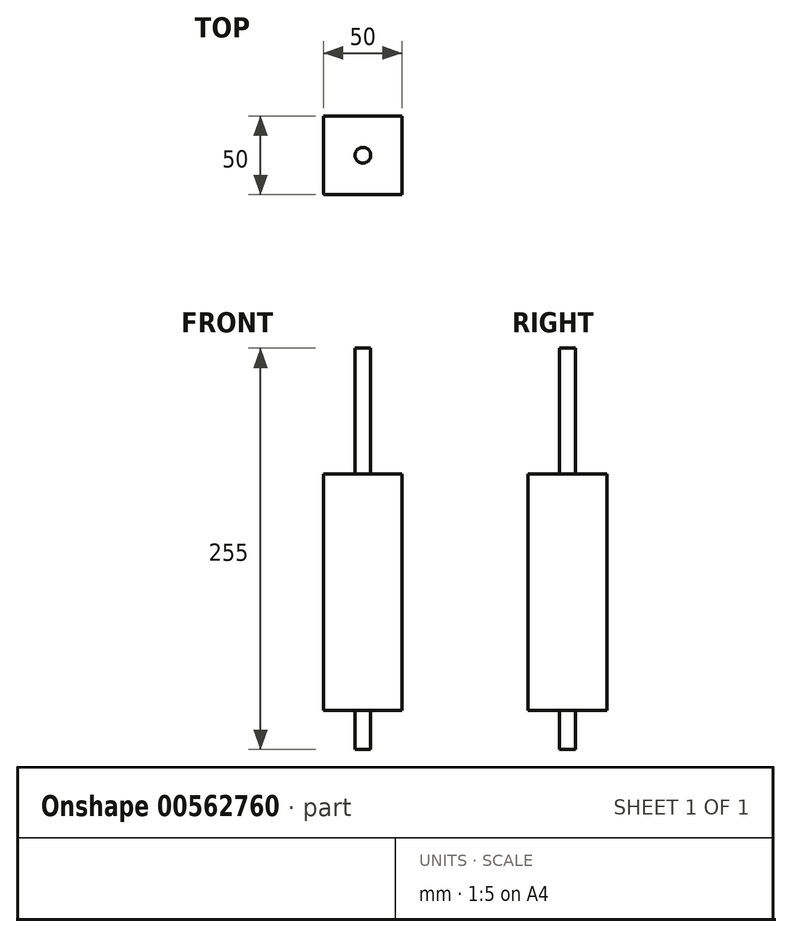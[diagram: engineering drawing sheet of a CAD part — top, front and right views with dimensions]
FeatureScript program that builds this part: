
annotation { "Feature Type Name" : "Feature", "Feature Type Description" : "" }
export const myFeature = defineFeature(function(context is Context, id is Id, definition is map)
    precondition{}
    {
        {
            var Q0;
            Q0=qCreatedBy(makeId("Top.planeOp"),FACE);
            var sketch = newSketch(context, id + "F0", { "sketchPlane" : qUnion([Q0])});
            skLineSegment(sketch, "E0.bottom", {"start": v(25, 25) * mm, "end": v(-25, 25) * mm});
            skLineSegment(sketch, "E0.top", {"start": v(25, -25) * mm, "end": v(-25, -25) * mm});
            skLineSegment(sketch, "E0.left", {"start": v(25, 25) * mm, "end": v(25, -25) * mm});
            skLineSegment(sketch, "E0.right", {"start": v(-25, 25) * mm, "end": v(-25, -25) * mm});
            skPoint(sketch, "E0.middle", {"position": v(0, 0) * mm});
            skSolve(sketch);
        }
        {
            var Q0;
            Q0=makeQuery(id+"F0.imprint","IMPRINT",FACE,{"disambiguationData":[TD([[makeQuery(id+"F0.imprint","IMPRINT",EDGE,{"derivedFrom":sQuery(id+"F0.wireOp",EDGE,"E0.bottom")}),1.0]])]});
            extrude(context, id + "F1", {"entities" : qUnion([Q0]), "endBound" : BoundingType.SYMMETRIC, "depth" : 150 * mm, "offsetDistance" : 25 * mm});
        }
        {
            var Q0;
            Q0=makeQuery(id+"F1.opExtrude","CAP_FACE",FACE,{"disambiguationData":[OSD([sQuery(id+"F0.wireOp",EDGE,"E0.bottom"),sQuery(id+"F0.wireOp",EDGE,"E0.top"),sQuery(id+"F0.wireOp",EDGE,"E0.left"),sQuery(id+"F0.wireOp",EDGE,"E0.right")])],"isStart":false});
            var sketch = newSketch(context, id + "F2", { "sketchPlane" : qUnion([Q0])});
            skCircle(sketch, "E1", {"center": v(0, 0) * mm, "radius": 5 * mm});
            skSolve(sketch);
        }
        {
            var Q0;
            Q0 = qSketchRegion(id + "F2", true);
            extrude(context, id + "F3", {"entities" : qUnion([Q0]), "operationType" : NewBodyOperationType.ADD, "depth" : 80 * mm, "offsetDistance" : 25 * mm});
        }
        {
            var Q0;
            Q0=makeQuery(id+"F1.opExtrude","CAP_FACE",FACE,{"disambiguationData":[OSD([sQuery(id+"F0.wireOp",EDGE,"E0.bottom"),sQuery(id+"F0.wireOp",EDGE,"E0.top"),sQuery(id+"F0.wireOp",EDGE,"E0.left"),sQuery(id+"F0.wireOp",EDGE,"E0.right")])],"isStart":true});
            var sketch = newSketch(context, id + "F4", { "sketchPlane" : qUnion([Q0])});
            skCircle(sketch, "E2", {"center": v(0, 0) * mm, "radius": 5 * mm});
            skSolve(sketch);
        }
        {
            var Q0;
            Q0 = qSketchRegion(id + "F4", true);
            extrude(context, id + "F5", {"entities" : qUnion([Q0]), "operationType" : NewBodyOperationType.ADD, "depth" : 25 * mm, "offsetDistance" : 25 * mm});
        }
    });
